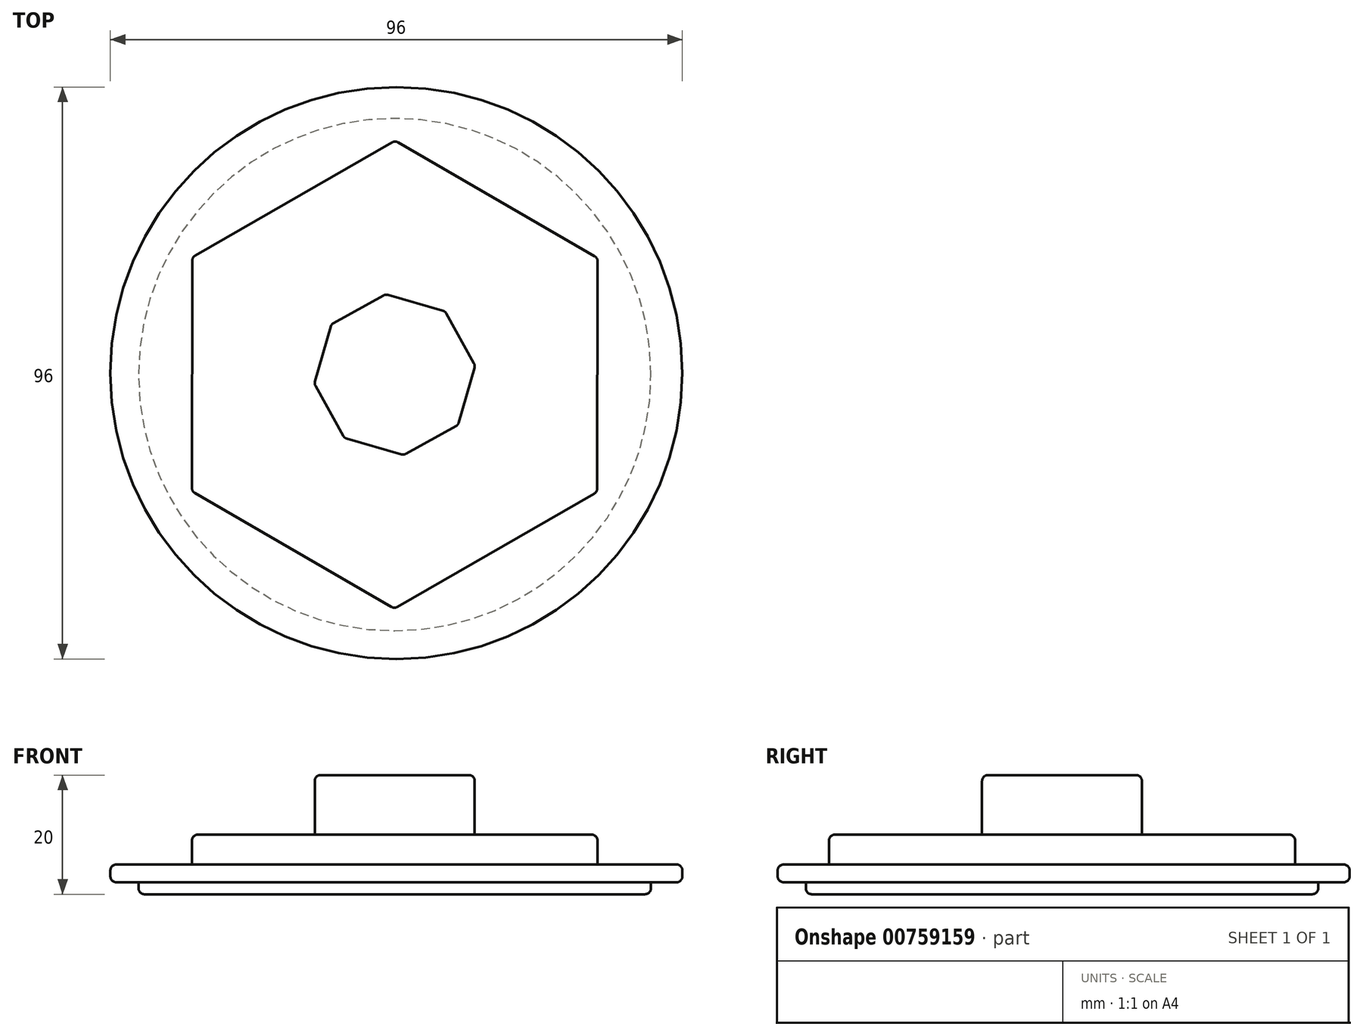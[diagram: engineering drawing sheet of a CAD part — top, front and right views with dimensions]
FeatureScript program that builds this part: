
annotation { "Feature Type Name" : "Feature", "Feature Type Description" : "" }
export const myFeature = defineFeature(function(context is Context, id is Id, definition is map)
    precondition{}
    {
        {
            var Q0;
            Q0=qCreatedBy(makeId("Top.planeOp"),FACE);
            var sketch = newSketch(context, id + "F0", { "sketchPlane" : qUnion([Q0])});
            skCircle(sketch, "E0", {"center": v(0.27, 0.27) * mm, "radius": 48 * mm});
            skSolve(sketch);
        }
        {
            var Q0;
            Q0=makeQuery(id+"F0.imprint","IMPRINT",FACE,{"disambiguationData":[TD([[makeQuery(id+"F0.imprint","IMPRINT",EDGE,{"derivedFrom":sQuery(id+"F0.wireOp",EDGE,"E0")}),1.0]])]});
            extrude(context, id + "F1", {"entities" : qUnion([Q0]), "depth" : 3 * mm, "offsetDistance" : 25 * mm});
        }
        {
            var Q0;
            Q0=makeQuery(id+"F1.opExtrude","CAP_FACE",FACE,{"disambiguationData":[OSD([sQuery(id+"F0.wireOp",EDGE,"E0")])],"isStart":false});
            var sketch = newSketch(context, id + "F2", { "sketchPlane" : qUnion([Q0])});
            skCircle(sketch, "E1.cCircle", {"center": v(0, 0) * mm, "radius": 34.02 * mm, "construction": true});
            skLineSegment(sketch, "E1.0", {"start": v(33.99, -19.7) * mm, "end": v(-0.06, -39.28) * mm});
            skLineSegment(sketch, "E1.1", {"start": v(-0.06, -39.28) * mm, "end": v(-34.05, -19.6) * mm});
            skLineSegment(sketch, "E1.2", {"start": v(-34.05, -19.6) * mm, "end": v(-33.99, 19.7) * mm});
            skLineSegment(sketch, "E1.3", {"start": v(-33.99, 19.7) * mm, "end": v(0.06, 39.28) * mm});
            skLineSegment(sketch, "E1.4", {"start": v(0.06, 39.28) * mm, "end": v(34.05, 19.6) * mm});
            skLineSegment(sketch, "E1.5", {"start": v(34.05, 19.6) * mm, "end": v(33.99, -19.7) * mm});
            skPoint(sketch, "E1.0.midPoint", {"position": v(16.97, -29.49) * mm});
            skSolve(sketch);
        }
        {
            var Q0;
            Q0=makeQuery(id+"F2.imprint","IMPRINT",FACE,{"disambiguationData":[TD([[makeQuery(id+"F2.imprint","IMPRINT",EDGE,{"derivedFrom":sQuery(id+"F2.wireOp",EDGE,"E1.0")}),-1.0]])]});
            extrude(context, id + "F3", {"entities" : qUnion([Q0]), "operationType" : NewBodyOperationType.ADD, "depth" : 5 * mm, "offsetDistance" : 25 * mm});
        }
        {
            var Q0;
            Q0=makeQuery(id+"F3.opExtrude","CAP_FACE",FACE,{"disambiguationData":[OSD([sQuery(id+"F2.wireOp",EDGE,"E1.0"),sQuery(id+"F2.wireOp",EDGE,"E1.1"),sQuery(id+"F2.wireOp",EDGE,"E1.2"),sQuery(id+"F2.wireOp",EDGE,"E1.3"),sQuery(id+"F2.wireOp",EDGE,"E1.4"),sQuery(id+"F2.wireOp",EDGE,"E1.5")])],"isStart":false});
            var sketch = newSketch(context, id + "F4", { "sketchPlane" : qUnion([Q0])});
            skCircle(sketch, "E2.cCircle", {"center": v(0, 0) * mm, "radius": 12.55 * mm, "construction": true});
            skLineSegment(sketch, "E2.0", {"start": v(10.63, -8.46) * mm, "end": v(1.53, -13.5) * mm});
            skLineSegment(sketch, "E2.1", {"start": v(1.53, -13.5) * mm, "end": v(-8.46, -10.63) * mm});
            skLineSegment(sketch, "E2.2", {"start": v(-8.46, -10.63) * mm, "end": v(-13.5, -1.53) * mm});
            skLineSegment(sketch, "E2.3", {"start": v(-13.5, -1.53) * mm, "end": v(-10.63, 8.46) * mm});
            skLineSegment(sketch, "E2.4", {"start": v(-10.63, 8.46) * mm, "end": v(-1.53, 13.5) * mm});
            skLineSegment(sketch, "E2.5", {"start": v(-1.53, 13.5) * mm, "end": v(8.46, 10.63) * mm});
            skLineSegment(sketch, "E2.6", {"start": v(8.46, 10.63) * mm, "end": v(13.5, 1.53) * mm});
            skLineSegment(sketch, "E2.7", {"start": v(13.5, 1.53) * mm, "end": v(10.63, -8.46) * mm});
            skPoint(sketch, "E2.0.midPoint", {"position": v(6.08, -10.98) * mm});
            skSolve(sketch);
        }
        {
            var Q0;
            Q0=makeQuery(id+"F4.imprint","IMPRINT",FACE,{"disambiguationData":[TD([[makeQuery(id+"F4.imprint","IMPRINT",EDGE,{"derivedFrom":sQuery(id+"F4.wireOp",EDGE,"E2.0")}),-1.0]])]});
            extrude(context, id + "F5", {"entities" : qUnion([Q0]), "operationType" : NewBodyOperationType.ADD, "depth" : 10 * mm, "offsetDistance" : 25 * mm});
        }
        {
            var Q0;
            Q0=makeQuery(id+"F1.opExtrude","CAP_FACE",FACE,{"disambiguationData":[OSD([sQuery(id+"F0.wireOp",EDGE,"E0")])],"isStart":true});
            var sketch = newSketch(context, id + "F6", { "sketchPlane" : qUnion([Q0])});
            skCircle(sketch, "E3", {"center": v(0, 0) * mm, "radius": 43 * mm});
            skSolve(sketch);
        }
        {
            var Q0;
            Q0=makeQuery(id+"F6.imprint","IMPRINT",FACE,{"disambiguationData":[TD([[makeQuery(id+"F6.imprint","IMPRINT",EDGE,{"derivedFrom":sQuery(id+"F6.wireOp",EDGE,"E3")}),1.0]])]});
            extrude(context, id + "F7", {"entities" : qUnion([Q0]), "operationType" : NewBodyOperationType.ADD, "depth" : 2 * mm, "offsetDistance" : 25 * mm});
        }
        {
            var Q0;
            Q0=makeQuery(id+"F3.opExtrude","CAP_EDGE",EDGE,{"disambiguationData":[OSD([sQuery(id+"F2.wireOp",EDGE,"E1.3")])],"isStart":false});
            var Q1;
            Q1=makeQuery(id+"F3.opExtrude","CAP_EDGE",EDGE,{"disambiguationData":[OSD([sQuery(id+"F2.wireOp",EDGE,"E1.2")])],"isStart":false});
            var Q2;
            Q2=makeQuery(id+"F3.opExtrude","CAP_EDGE",EDGE,{"disambiguationData":[OSD([sQuery(id+"F2.wireOp",EDGE,"E1.1")])],"isStart":false});
            var Q3;
            Q3=makeQuery(id+"F3.opExtrude","CAP_EDGE",EDGE,{"disambiguationData":[OSD([sQuery(id+"F2.wireOp",EDGE,"E1.0")])],"isStart":false});
            var Q4;
            Q4=makeQuery(id+"F3.opExtrude","CAP_EDGE",EDGE,{"disambiguationData":[OSD([sQuery(id+"F2.wireOp",EDGE,"E1.5")])],"isStart":false});
            var Q5;
            Q5=makeQuery(id+"F3.opExtrude","CAP_EDGE",EDGE,{"disambiguationData":[OSD([sQuery(id+"F2.wireOp",EDGE,"E1.4")])],"isStart":false});
            var Q6;
            Q6=makeQuery(id+"F5.opExtrude","CAP_EDGE",EDGE,{"disambiguationData":[OSD([sQuery(id+"F4.wireOp",EDGE,"E2.4")])],"isStart":false});
            var Q7;
            Q7=makeQuery(id+"F5.opExtrude","CAP_EDGE",EDGE,{"disambiguationData":[OSD([sQuery(id+"F4.wireOp",EDGE,"E2.3")])],"isStart":false});
            var Q8;
            Q8=makeQuery(id+"F5.opExtrude","CAP_EDGE",EDGE,{"disambiguationData":[OSD([sQuery(id+"F4.wireOp",EDGE,"E2.2")])],"isStart":false});
            var Q9;
            Q9=makeQuery(id+"F5.opExtrude","CAP_EDGE",EDGE,{"disambiguationData":[OSD([sQuery(id+"F4.wireOp",EDGE,"E2.1")])],"isStart":false});
            var Q10;
            Q10=makeQuery(id+"F5.opExtrude","CAP_EDGE",EDGE,{"disambiguationData":[OSD([sQuery(id+"F4.wireOp",EDGE,"E2.0")])],"isStart":false});
            var Q11;
            Q11=makeQuery(id+"F5.opExtrude","CAP_EDGE",EDGE,{"disambiguationData":[OSD([sQuery(id+"F4.wireOp",EDGE,"E2.7")])],"isStart":false});
            var Q12;
            Q12=makeQuery(id+"F5.opExtrude","CAP_EDGE",EDGE,{"disambiguationData":[OSD([sQuery(id+"F4.wireOp",EDGE,"E2.6")])],"isStart":false});
            var Q13;
            Q13=makeQuery(id+"F5.opExtrude","CAP_EDGE",EDGE,{"disambiguationData":[OSD([sQuery(id+"F4.wireOp",EDGE,"E2.5")])],"isStart":false});
            var Q14;
            Q14=makeQuery(id+"F5.opExtrude","SWEPT_EDGE",EDGE,{"disambiguationData":[OSD([sQuery(id+"F4.wireOp",EDGE,"E2.1"),sQuery(id+"F4.wireOp",EDGE,"E2.2")])]});
            var Q15;
            Q15=makeQuery(id+"F5.opExtrude","SWEPT_EDGE",EDGE,{"disambiguationData":[OSD([sQuery(id+"F4.wireOp",EDGE,"E2.0"),sQuery(id+"F4.wireOp",EDGE,"E2.1")])]});
            var Q16;
            Q16=makeQuery(id+"F5.opExtrude","SWEPT_EDGE",EDGE,{"disambiguationData":[OSD([sQuery(id+"F4.wireOp",EDGE,"E2.0"),sQuery(id+"F4.wireOp",EDGE,"E2.7")])]});
            var Q17;
            Q17=makeQuery(id+"F5.opExtrude","SWEPT_EDGE",EDGE,{"disambiguationData":[OSD([sQuery(id+"F4.wireOp",EDGE,"E2.6"),sQuery(id+"F4.wireOp",EDGE,"E2.7")])]});
            var Q18;
            Q18=makeQuery(id+"F5.opExtrude","SWEPT_EDGE",EDGE,{"disambiguationData":[OSD([sQuery(id+"F4.wireOp",EDGE,"E2.5"),sQuery(id+"F4.wireOp",EDGE,"E2.6")])]});
            var Q19;
            Q19=makeQuery(id+"F5.opExtrude","SWEPT_EDGE",EDGE,{"disambiguationData":[OSD([sQuery(id+"F4.wireOp",EDGE,"E2.4"),sQuery(id+"F4.wireOp",EDGE,"E2.5")])]});
            var Q20;
            Q20=makeQuery(id+"F5.opExtrude","SWEPT_EDGE",EDGE,{"disambiguationData":[OSD([sQuery(id+"F4.wireOp",EDGE,"E2.3"),sQuery(id+"F4.wireOp",EDGE,"E2.4")])]});
            var Q21;
            Q21=makeQuery(id+"F5.opExtrude","SWEPT_EDGE",EDGE,{"disambiguationData":[OSD([sQuery(id+"F4.wireOp",EDGE,"E2.2"),sQuery(id+"F4.wireOp",EDGE,"E2.3")])]});
            var Q22;
            Q22=makeQuery(id+"F3.opExtrude","SWEPT_EDGE",EDGE,{"disambiguationData":[OSD([sQuery(id+"F2.wireOp",EDGE,"E1.3"),sQuery(id+"F2.wireOp",EDGE,"E1.4")])]});
            var Q23;
            Q23=makeQuery(id+"F3.opExtrude","SWEPT_EDGE",EDGE,{"disambiguationData":[OSD([sQuery(id+"F2.wireOp",EDGE,"E1.4"),sQuery(id+"F2.wireOp",EDGE,"E1.5")])]});
            var Q24;
            Q24=makeQuery(id+"F3.opExtrude","SWEPT_EDGE",EDGE,{"disambiguationData":[OSD([sQuery(id+"F2.wireOp",EDGE,"E1.0"),sQuery(id+"F2.wireOp",EDGE,"E1.5")])]});
            var Q25;
            Q25=makeQuery(id+"F3.opExtrude","SWEPT_EDGE",EDGE,{"disambiguationData":[OSD([sQuery(id+"F2.wireOp",EDGE,"E1.0"),sQuery(id+"F2.wireOp",EDGE,"E1.1")])]});
            var Q26;
            Q26=makeQuery(id+"F3.opExtrude","SWEPT_EDGE",EDGE,{"disambiguationData":[OSD([sQuery(id+"F2.wireOp",EDGE,"E1.1"),sQuery(id+"F2.wireOp",EDGE,"E1.2")])]});
            var Q27;
            Q27=makeQuery(id+"F3.opExtrude","SWEPT_EDGE",EDGE,{"disambiguationData":[OSD([sQuery(id+"F2.wireOp",EDGE,"E1.2"),sQuery(id+"F2.wireOp",EDGE,"E1.3")])]});
            var Q28;
            Q28=makeQuery(id+"F1.opExtrude","CAP_EDGE",EDGE,{"disambiguationData":[OSD([sQuery(id+"F0.wireOp",EDGE,"E0")])],"isStart":false});
            var Q29;
            Q29=makeQuery(id+"F1.opExtrude","CAP_EDGE",EDGE,{"disambiguationData":[OSD([sQuery(id+"F0.wireOp",EDGE,"E0")])],"isStart":true});
            var Q30;
            Q30=makeQuery(id+"F7.opExtrude","CAP_EDGE",EDGE,{"disambiguationData":[OSD([sQuery(id+"F6.wireOp",EDGE,"E3")])],"isStart":false});
            fillet(context, id + "F8", {"entities" : qUnion([Q0, Q1, Q2, Q3, Q4, Q5, Q6, Q7, Q8, Q9, Q10, Q11, Q12, Q13, Q14, Q15, Q16, Q17, Q18, Q19, Q20, Q21, Q22, Q23, Q24, Q25, Q26, Q27, Q28, Q29, Q30]), "radius" : 1 * mm, "tangentPropagation" : true, "allowEdgeOverflow" : false});
        }
    });
